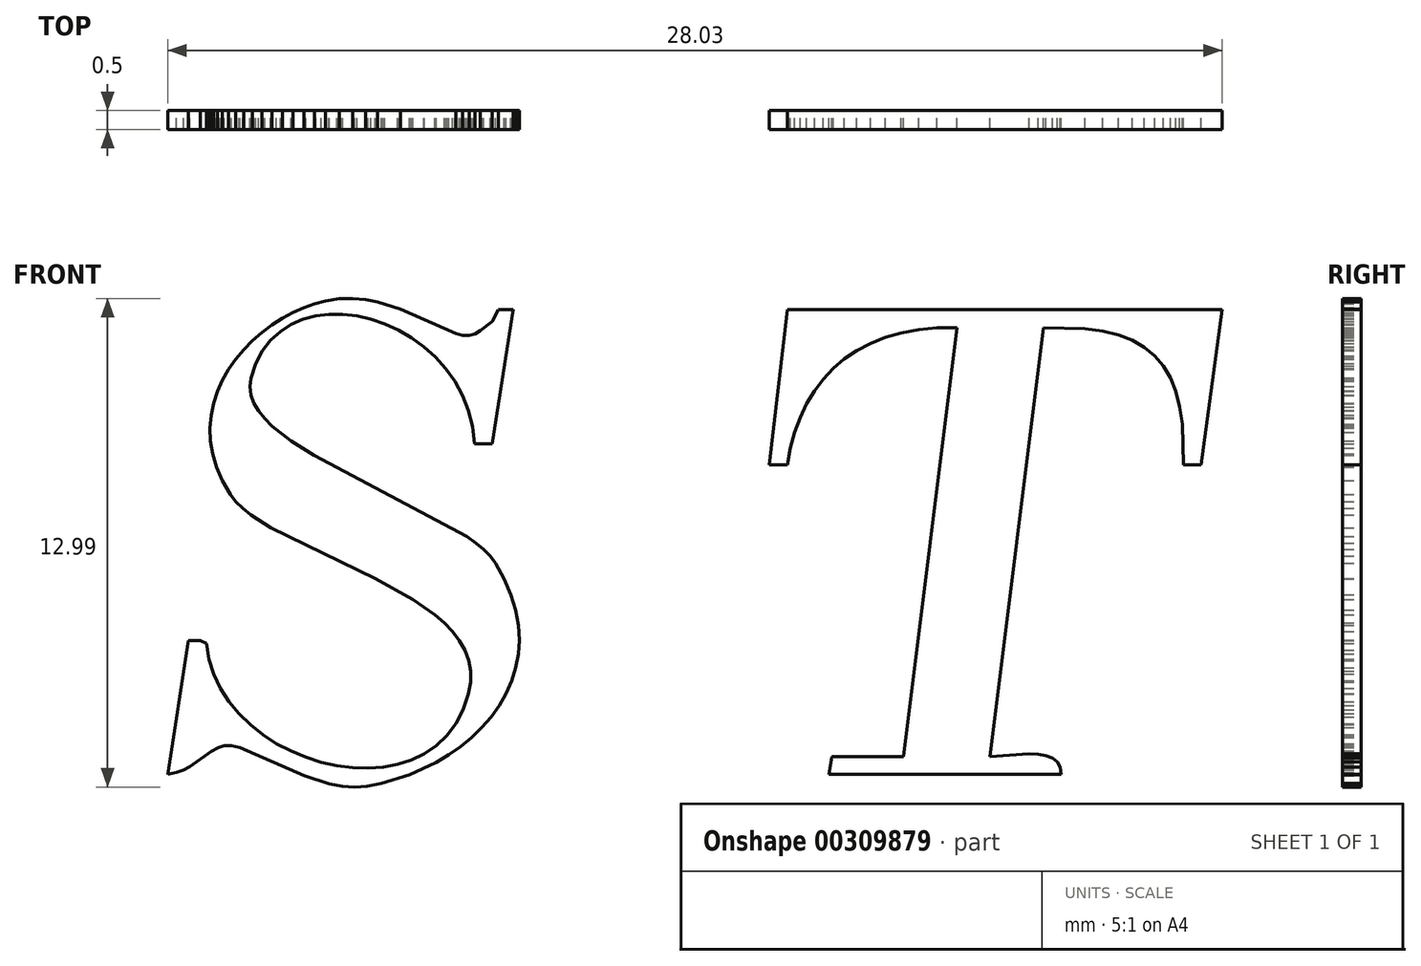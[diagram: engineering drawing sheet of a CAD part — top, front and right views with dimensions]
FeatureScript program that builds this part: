
annotation { "Feature Type Name" : "Feature", "Feature Type Description" : "" }
export const myFeature = defineFeature(function(context is Context, id is Id, definition is map)
    precondition{}
    {
        {
            var Q0;
            Q0=qCreatedBy(makeId("Front.planeOp"),FACE);
            var sketch = newSketch(context, id + "F0", { "sketchPlane" : qUnion([Q0])});
            skPoint(sketch, "E0.0", {"position": v(18.56, 6.4) * mm});
            skPoint(sketch, "E1.0", {"position": v(18, 2.28) * mm});
            skPoint(sketch, "E2.0", {"position": v(17.53, 2.28) * mm});
            skPoint(sketch, "E3.0", {"position": v(17.5, 3.36) * mm});
            skPoint(sketch, "E4.0", {"position": v(17.43, 3.82) * mm});
            skPoint(sketch, "E5.0", {"position": v(17.33, 4.23) * mm});
            skPoint(sketch, "E6.0", {"position": v(17.18, 4.6) * mm});
            skPoint(sketch, "E7.0", {"position": v(17, 4.9) * mm});
            skPoint(sketch, "E8.0", {"position": v(16.77, 5.18) * mm});
            skPoint(sketch, "E9.0", {"position": v(16.5, 5.4) * mm});
            skPoint(sketch, "E10.0", {"position": v(16.17, 5.59) * mm});
            skPoint(sketch, "E11.0", {"position": v(15.8, 5.73) * mm});
            skPoint(sketch, "E12.0", {"position": v(15.38, 5.83) * mm});
            skPoint(sketch, "E13.0", {"position": v(14.91, 5.9) * mm});
            skPoint(sketch, "E14.0", {"position": v(13.8, 5.93) * mm});
            skPoint(sketch, "E15.0", {"position": v(12.38, -5.48) * mm});
            skPoint(sketch, "E16.0", {"position": v(13.43, -5.4) * mm});
            skPoint(sketch, "E17.0", {"position": v(13.66, -5.42) * mm});
            skPoint(sketch, "E18.0", {"position": v(13.87, -5.46) * mm});
            skPoint(sketch, "E19.0", {"position": v(14.04, -5.52) * mm});
            skPoint(sketch, "E20.0", {"position": v(14.18, -5.62) * mm});
            skPoint(sketch, "E21.0", {"position": v(14.26, -5.76) * mm});
            skPoint(sketch, "E22.0", {"position": v(14.28, -5.95) * mm});
            skPoint(sketch, "E23.0", {"position": v(8.1, -5.95) * mm});
            skPoint(sketch, "E24.0", {"position": v(8.19, -5.48) * mm});
            skPoint(sketch, "E25.0", {"position": v(10.09, -5.48) * mm});
            skPoint(sketch, "E26.0", {"position": v(11.51, 5.93) * mm});
            skPoint(sketch, "E27.0", {"position": v(10.98, 5.92) * mm});
            skPoint(sketch, "E28.0", {"position": v(10.49, 5.87) * mm});
            skPoint(sketch, "E29.0", {"position": v(10.03, 5.79) * mm});
            skPoint(sketch, "E30.0", {"position": v(9.6, 5.67) * mm});
            skPoint(sketch, "E31.0", {"position": v(9.2, 5.51) * mm});
            skPoint(sketch, "E32.0", {"position": v(8.84, 5.32) * mm});
            skPoint(sketch, "E33.0", {"position": v(8.52, 5.1) * mm});
            skPoint(sketch, "E34.0", {"position": v(8.22, 4.84) * mm});
            skPoint(sketch, "E35.0", {"position": v(7.95, 4.56) * mm});
            skPoint(sketch, "E36.0", {"position": v(7.72, 4.25) * mm});
            skPoint(sketch, "E37.0", {"position": v(7.52, 3.9) * mm});
            skPoint(sketch, "E38.0", {"position": v(7.34, 3.54) * mm});
            skPoint(sketch, "E39.0", {"position": v(7.2, 3.14) * mm});
            skPoint(sketch, "E40.0", {"position": v(7.08, 2.72) * mm});
            skPoint(sketch, "E41.0", {"position": v(7, 2.28) * mm});
            skPoint(sketch, "E42.0", {"position": v(6.52, 2.28) * mm});
            skPoint(sketch, "E43.0", {"position": v(7, 6.4) * mm});
            skPoint(sketch, "E44.0", {"position": v(-0.29, 6.4) * mm});
            skPoint(sketch, "E45.0", {"position": v(-0.84, 2.84) * mm});
            skPoint(sketch, "E46.0", {"position": v(-1.32, 2.84) * mm});
            skPoint(sketch, "E47.0", {"position": v(-1.37, 3.3) * mm});
            skPoint(sketch, "E48.0", {"position": v(-1.48, 3.72) * mm});
            skPoint(sketch, "E49.0", {"position": v(-1.64, 4.13) * mm});
            skPoint(sketch, "E50.0", {"position": v(-1.84, 4.5) * mm});
            skPoint(sketch, "E51.0", {"position": v(-2.08, 4.84) * mm});
            skPoint(sketch, "E52.0", {"position": v(-2.36, 5.14) * mm});
            skPoint(sketch, "E53.0", {"position": v(-0.68, 6.4) * mm});
            skPoint(sketch, "E54.0", {"position": v(-0.84, 6.08) * mm});
            skPoint(sketch, "E55.0", {"position": v(-1.16, 5.85) * mm});
            skPoint(sketch, "E56.0", {"position": v(-1.3, 5.76) * mm});
            skPoint(sketch, "E57.0", {"position": v(-1.46, 5.72) * mm});
            skPoint(sketch, "E58.0", {"position": v(-1.63, 5.72) * mm});
            skPoint(sketch, "E59.0", {"position": v(-1.82, 5.77) * mm});
            skPoint(sketch, "E60.0", {"position": v(-3.28, 6.41) * mm});
            skPoint(sketch, "E61.0", {"position": v(-2.66, 5.42) * mm});
            skPoint(sketch, "E62.0", {"position": v(-2.99, 5.66) * mm});
            skPoint(sketch, "E63.0", {"position": v(-3.34, 5.86) * mm});
            skPoint(sketch, "E64.0", {"position": v(-3.7, 6.03) * mm});
            skPoint(sketch, "E65.0", {"position": v(-4.07, 6.15) * mm});
            skPoint(sketch, "E66.0", {"position": v(-4.44, 6.24) * mm});
            skPoint(sketch, "E67.0", {"position": v(-4.82, 6.28) * mm});
            skPoint(sketch, "E68.0", {"position": v(-4.22, 6.67) * mm});
            skPoint(sketch, "E69.0", {"position": v(-3.9, 6.61) * mm});
            skPoint(sketch, "E70.0", {"position": v(-4.56, 6.7) * mm});
            skPoint(sketch, "E71.0", {"position": v(-4.91, 6.7) * mm});
            skPoint(sketch, "E72.0", {"position": v(-5.18, 6.28) * mm});
            skPoint(sketch, "E73.0", {"position": v(-5.28, 6.64) * mm});
            skPoint(sketch, "E74.0", {"position": v(-5.57, 6.56) * mm});
            skPoint(sketch, "E75.0", {"position": v(-5.54, 6.24) * mm});
            skPoint(sketch, "E76.0", {"position": v(-5.88, 6.15) * mm});
            skPoint(sketch, "E77.0", {"position": v(-5.86, 6.46) * mm});
            skPoint(sketch, "E78.0", {"position": v(-6.14, 6.33) * mm});
            skPoint(sketch, "E79.0", {"position": v(-6.2, 6.01) * mm});
            skPoint(sketch, "E80.0", {"position": v(-6.43, 6.18) * mm});
            skPoint(sketch, "E81.0", {"position": v(-6.48, 5.83) * mm});
            skPoint(sketch, "E82.0", {"position": v(-6.7, 6) * mm});
            skPoint(sketch, "E83.0", {"position": v(-6.97, 5.8) * mm});
            skPoint(sketch, "E84.0", {"position": v(-6.73, 5.6) * mm});
            skPoint(sketch, "E85.0", {"position": v(-7.22, 5.58) * mm});
            skPoint(sketch, "E86.0", {"position": v(-6.95, 5.3) * mm});
            skPoint(sketch, "E87.0", {"position": v(-7.45, 5.35) * mm});
            skPoint(sketch, "E88.0", {"position": v(-7.13, 4.97) * mm});
            skPoint(sketch, "E89.0", {"position": v(-7.66, 5.1) * mm});
            skPoint(sketch, "E90.0", {"position": v(-7.26, 4.58) * mm});
            skPoint(sketch, "E91.0", {"position": v(-7.29, 4.36) * mm});
            skPoint(sketch, "E92.0", {"position": v(-7.26, 4.14) * mm});
            skPoint(sketch, "E93.0", {"position": v(-7.18, 3.92) * mm});
            skPoint(sketch, "E94.0", {"position": v(-7.06, 3.71) * mm});
            skPoint(sketch, "E95.0", {"position": v(-6.9, 3.5) * mm});
            skPoint(sketch, "E96.0", {"position": v(-6.7, 3.3) * mm});
            skPoint(sketch, "E97.0", {"position": v(-6.2, 2.91) * mm});
            skPoint(sketch, "E98.0", {"position": v(-5.59, 2.53) * mm});
            skPoint(sketch, "E99.0", {"position": v(-1.53, 0.38) * mm});
            skPoint(sketch, "E100.0", {"position": v(-1.28, 0.2) * mm});
            skPoint(sketch, "E101.0", {"position": v(-1.07, 0.03) * mm});
            skPoint(sketch, "E102.0", {"position": v(-0.9, -0.15) * mm});
            skPoint(sketch, "E103.0", {"position": v(-0.76, -0.33) * mm});
            skPoint(sketch, "E104.0", {"position": v(-0.53, -0.76) * mm});
            skPoint(sketch, "E105.0", {"position": v(-0.35, -1.18) * mm});
            skPoint(sketch, "E106.0", {"position": v(-0.22, -1.59) * mm});
            skPoint(sketch, "E107.0", {"position": v(-0.15, -1.99) * mm});
            skPoint(sketch, "E108.0", {"position": v(-0.13, -2.38) * mm});
            skPoint(sketch, "E109.0", {"position": v(-0.15, -2.75) * mm});
            skPoint(sketch, "E110.0", {"position": v(-0.22, -3.12) * mm});
            skPoint(sketch, "E111.0", {"position": v(-0.33, -3.47) * mm});
            skPoint(sketch, "E112.0", {"position": v(-0.48, -3.8) * mm});
            skPoint(sketch, "E113.0", {"position": v(-0.66, -4.12) * mm});
            skPoint(sketch, "E114.0", {"position": v(-0.88, -4.42) * mm});
            skPoint(sketch, "E115.0", {"position": v(-1.12, -4.7) * mm});
            skPoint(sketch, "E116.0", {"position": v(-1.4, -4.97) * mm});
            skPoint(sketch, "E117.0", {"position": v(-1.69, -5.21) * mm});
            skPoint(sketch, "E118.0", {"position": v(-2, -5.43) * mm});
            skPoint(sketch, "E119.0", {"position": v(-2.34, -5.64) * mm});
            skPoint(sketch, "E120.0", {"position": v(-3.04, -5.97) * mm});
            skPoint(sketch, "E121.0", {"position": v(-3.79, -6.2) * mm});
            skPoint(sketch, "E122.0", {"position": v(-4.17, -6.27) * mm});
            skPoint(sketch, "E123.0", {"position": v(-4.5, -6.3) * mm});
            skPoint(sketch, "E124.0", {"position": v(-4.84, -6.27) * mm});
            skPoint(sketch, "E125.0", {"position": v(-5.17, -6.2) * mm});
            skPoint(sketch, "E126.0", {"position": v(-5.84, -5.99) * mm});
            skPoint(sketch, "E127.0", {"position": v(-7.56, -5.24) * mm});
            skPoint(sketch, "E128.0", {"position": v(-6.2, -5.33) * mm});
            skPoint(sketch, "E129.0", {"position": v(-5.8, -5.5) * mm});
            skPoint(sketch, "E130.0", {"position": v(-5.4, -5.63) * mm});
            skPoint(sketch, "E131.0", {"position": v(-4.98, -5.72) * mm});
            skPoint(sketch, "E132.0", {"position": v(-4.56, -5.77) * mm});
            skPoint(sketch, "E133.0", {"position": v(-4.15, -5.79) * mm});
            skPoint(sketch, "E134.0", {"position": v(-3.75, -5.76) * mm});
            skPoint(sketch, "E135.0", {"position": v(-3.36, -5.68) * mm});
            skPoint(sketch, "E136.0", {"position": v(-3, -5.56) * mm});
            skPoint(sketch, "E137.0", {"position": v(-2.65, -5.4) * mm});
            skPoint(sketch, "E138.0", {"position": v(-2.33, -5.19) * mm});
            skPoint(sketch, "E139.0", {"position": v(-2.05, -4.92) * mm});
            skPoint(sketch, "E140.0", {"position": v(-1.81, -4.6) * mm});
            skPoint(sketch, "E141.0", {"position": v(-1.62, -4.24) * mm});
            skPoint(sketch, "E142.0", {"position": v(-1.48, -3.81) * mm});
            skPoint(sketch, "E143.0", {"position": v(-1.42, -3.5) * mm});
            skPoint(sketch, "E144.0", {"position": v(-1.42, -3.2) * mm});
            skPoint(sketch, "E145.0", {"position": v(-1.47, -2.92) * mm});
            skPoint(sketch, "E146.0", {"position": v(-1.57, -2.65) * mm});
            skPoint(sketch, "E147.0", {"position": v(-1.72, -2.4) * mm});
            skPoint(sketch, "E148.0", {"position": v(-1.9, -2.16) * mm});
            skPoint(sketch, "E149.0", {"position": v(-2.12, -1.93) * mm});
            skPoint(sketch, "E150.0", {"position": v(-2.37, -1.7) * mm});
            skPoint(sketch, "E151.0", {"position": v(-2.95, -1.3) * mm});
            skPoint(sketch, "E152.0", {"position": v(-3.96, -0.74) * mm});
            skPoint(sketch, "E153.0", {"position": v(-6.72, 0.6) * mm});
            skPoint(sketch, "E154.0", {"position": v(-7.26, 0.94) * mm});
            skPoint(sketch, "E155.0", {"position": v(-7.48, 1.12) * mm});
            skPoint(sketch, "E156.0", {"position": v(-7.67, 1.3) * mm});
            skPoint(sketch, "E157.0", {"position": v(-7.81, 1.5) * mm});
            skPoint(sketch, "E158.0", {"position": v(-8.02, 1.86) * mm});
            skPoint(sketch, "E159.0", {"position": v(-8.18, 2.22) * mm});
            skPoint(sketch, "E160.0", {"position": v(-8.28, 2.57) * mm});
            skPoint(sketch, "E161.0", {"position": v(-8.34, 2.92) * mm});
            skPoint(sketch, "E162.0", {"position": v(-8.35, 3.26) * mm});
            skPoint(sketch, "E163.0", {"position": v(-8.32, 3.6) * mm});
            skPoint(sketch, "E164.0", {"position": v(-8.25, 3.92) * mm});
            skPoint(sketch, "E165.0", {"position": v(-8.15, 4.23) * mm});
            skPoint(sketch, "E166.0", {"position": v(-8.02, 4.53) * mm});
            skPoint(sketch, "E167.0", {"position": v(-7.85, 4.82) * mm});
            skPoint(sketch, "E168.0", {"position": v(-7.77, -5.2) * mm});
            skPoint(sketch, "E169.0", {"position": v(-7.97, -5.19) * mm});
            skPoint(sketch, "E170.0", {"position": v(-8.13, -5.24) * mm});
            skPoint(sketch, "E171.0", {"position": v(-8.3, -5.34) * mm});
            skPoint(sketch, "E172.0", {"position": v(-8.89, -5.75) * mm});
            skPoint(sketch, "E173.0", {"position": v(-9.05, -5.83) * mm});
            skPoint(sketch, "E174.0", {"position": v(-9.24, -5.9) * mm});
            skPoint(sketch, "E175.0", {"position": v(-9.47, -5.95) * mm});
            skPoint(sketch, "E176.0", {"position": v(-8.92, -2.39) * mm});
            skPoint(sketch, "E177.0", {"position": v(-8.6, -2.39) * mm});
            skPoint(sketch, "E178.0", {"position": v(-8.45, -2.47) * mm});
            skPoint(sketch, "E179.0", {"position": v(-8.38, -2.89) * mm});
            skPoint(sketch, "E180.0", {"position": v(-8.25, -3.29) * mm});
            skPoint(sketch, "E181.0", {"position": v(-8.07, -3.66) * mm});
            skPoint(sketch, "E182.0", {"position": v(-7.85, -4.01) * mm});
            skPoint(sketch, "E183.0", {"position": v(-7.58, -4.34) * mm});
            skPoint(sketch, "E184.0", {"position": v(-7.28, -4.63) * mm});
            skPoint(sketch, "E185.0", {"position": v(-6.94, -4.9) * mm});
            skPoint(sketch, "E186.0", {"position": v(-6.58, -5.13) * mm});
            skLineSegment(sketch, "E187", {"start": v(7, 6.4) * mm, "end": v(18.56, 6.4) * mm});
            skLineSegment(sketch, "E188", {"start": v(18.56, 6.4) * mm, "end": v(18, 2.28) * mm});
            skLineSegment(sketch, "E189", {"start": v(18, 2.28) * mm, "end": v(17.53, 2.28) * mm});
            skLineSegment(sketch, "E190", {"start": v(17.53, 2.28) * mm, "end": v(17.5, 3.36) * mm});
            skLineSegment(sketch, "E191", {"start": v(17.5, 3.36) * mm, "end": v(17.43, 3.82) * mm});
            skLineSegment(sketch, "E192", {"start": v(17.43, 3.82) * mm, "end": v(17.33, 4.23) * mm});
            skLineSegment(sketch, "E193", {"start": v(17.33, 4.23) * mm, "end": v(17.18, 4.6) * mm});
            skLineSegment(sketch, "E194", {"start": v(17.18, 4.6) * mm, "end": v(17, 4.9) * mm});
            skLineSegment(sketch, "E195", {"start": v(17, 4.9) * mm, "end": v(16.77, 5.18) * mm});
            skLineSegment(sketch, "E196", {"start": v(16.77, 5.18) * mm, "end": v(16.5, 5.4) * mm});
            skLineSegment(sketch, "E197", {"start": v(16.5, 5.4) * mm, "end": v(16.17, 5.59) * mm});
            skLineSegment(sketch, "E198", {"start": v(16.17, 5.59) * mm, "end": v(15.8, 5.73) * mm});
            skLineSegment(sketch, "E199", {"start": v(15.8, 5.73) * mm, "end": v(15.38, 5.83) * mm});
            skLineSegment(sketch, "E200", {"start": v(15.38, 5.83) * mm, "end": v(14.91, 5.9) * mm});
            skLineSegment(sketch, "E201", {"start": v(14.91, 5.9) * mm, "end": v(13.8, 5.93) * mm});
            skLineSegment(sketch, "E202", {"start": v(13.8, 5.93) * mm, "end": v(12.38, -5.48) * mm});
            skLineSegment(sketch, "E203", {"start": v(12.38, -5.48) * mm, "end": v(13.43, -5.4) * mm});
            skLineSegment(sketch, "E204", {"start": v(13.43, -5.4) * mm, "end": v(13.66, -5.42) * mm});
            skLineSegment(sketch, "E205", {"start": v(13.66, -5.42) * mm, "end": v(13.87, -5.46) * mm});
            skLineSegment(sketch, "E206", {"start": v(13.87, -5.46) * mm, "end": v(14.04, -5.52) * mm});
            skLineSegment(sketch, "E207", {"start": v(14.04, -5.52) * mm, "end": v(14.18, -5.62) * mm});
            skLineSegment(sketch, "E208", {"start": v(14.18, -5.62) * mm, "end": v(14.26, -5.76) * mm});
            skLineSegment(sketch, "E209", {"start": v(14.26, -5.76) * mm, "end": v(14.28, -5.95) * mm});
            skLineSegment(sketch, "E210", {"start": v(14.28, -5.95) * mm, "end": v(8.1, -5.95) * mm});
            skLineSegment(sketch, "E211", {"start": v(8.1, -5.95) * mm, "end": v(8.19, -5.48) * mm});
            skLineSegment(sketch, "E212", {"start": v(8.19, -5.48) * mm, "end": v(10.09, -5.48) * mm});
            skLineSegment(sketch, "E213", {"start": v(11.51, 5.93) * mm, "end": v(10.09, -5.48) * mm});
            skLineSegment(sketch, "E214", {"start": v(11.51, 5.93) * mm, "end": v(10.98, 5.92) * mm});
            skLineSegment(sketch, "E215", {"start": v(10.98, 5.92) * mm, "end": v(10.49, 5.87) * mm});
            skLineSegment(sketch, "E216", {"start": v(10.49, 5.87) * mm, "end": v(10.03, 5.79) * mm});
            skLineSegment(sketch, "E217", {"start": v(10.03, 5.79) * mm, "end": v(9.6, 5.67) * mm});
            skLineSegment(sketch, "E218", {"start": v(9.6, 5.67) * mm, "end": v(9.2, 5.51) * mm});
            skLineSegment(sketch, "E219", {"start": v(9.2, 5.51) * mm, "end": v(8.84, 5.32) * mm});
            skLineSegment(sketch, "E220", {"start": v(8.84, 5.32) * mm, "end": v(8.52, 5.1) * mm});
            skLineSegment(sketch, "E221", {"start": v(8.52, 5.1) * mm, "end": v(8.22, 4.84) * mm});
            skLineSegment(sketch, "E222", {"start": v(8.22, 4.84) * mm, "end": v(7.95, 4.56) * mm});
            skLineSegment(sketch, "E223", {"start": v(7.95, 4.56) * mm, "end": v(7.72, 4.25) * mm});
            skLineSegment(sketch, "E224", {"start": v(7.72, 4.25) * mm, "end": v(7.52, 3.9) * mm});
            skLineSegment(sketch, "E225", {"start": v(7.52, 3.9) * mm, "end": v(7.34, 3.54) * mm});
            skLineSegment(sketch, "E226", {"start": v(7.34, 3.54) * mm, "end": v(7.2, 3.14) * mm});
            skLineSegment(sketch, "E227", {"start": v(7.2, 3.14) * mm, "end": v(7.08, 2.72) * mm});
            skLineSegment(sketch, "E228", {"start": v(7.08, 2.72) * mm, "end": v(7, 2.28) * mm});
            skLineSegment(sketch, "E229", {"start": v(7, 2.28) * mm, "end": v(6.52, 2.28) * mm});
            skLineSegment(sketch, "E230", {"start": v(7, 6.4) * mm, "end": v(6.52, 2.28) * mm});
            skLineSegment(sketch, "E231", {"start": v(-0.29, 6.4) * mm, "end": v(-0.84, 2.84) * mm});
            skLineSegment(sketch, "E232", {"start": v(-0.84, 2.84) * mm, "end": v(-1.32, 2.84) * mm});
            skLineSegment(sketch, "E233", {"start": v(-1.32, 2.84) * mm, "end": v(-1.37, 3.3) * mm});
            skLineSegment(sketch, "E234", {"start": v(-1.37, 3.3) * mm, "end": v(-1.48, 3.72) * mm});
            skLineSegment(sketch, "E235", {"start": v(-1.48, 3.72) * mm, "end": v(-1.64, 4.13) * mm});
            skLineSegment(sketch, "E236", {"start": v(-1.64, 4.13) * mm, "end": v(-1.84, 4.5) * mm});
            skLineSegment(sketch, "E237", {"start": v(-1.84, 4.5) * mm, "end": v(-2.08, 4.84) * mm});
            skLineSegment(sketch, "E238", {"start": v(-2.08, 4.84) * mm, "end": v(-2.36, 5.14) * mm});
            skLineSegment(sketch, "E239", {"start": v(-2.36, 5.14) * mm, "end": v(-2.66, 5.42) * mm});
            skLineSegment(sketch, "E240", {"start": v(-0.29, 6.4) * mm, "end": v(-0.68, 6.4) * mm});
            skLineSegment(sketch, "E241", {"start": v(-0.68, 6.4) * mm, "end": v(-0.84, 6.08) * mm});
            skLineSegment(sketch, "E242", {"start": v(-0.84, 6.08) * mm, "end": v(-1.16, 5.85) * mm});
            skLineSegment(sketch, "E243", {"start": v(-1.16, 5.85) * mm, "end": v(-1.3, 5.76) * mm});
            skLineSegment(sketch, "E244", {"start": v(-1.3, 5.76) * mm, "end": v(-1.46, 5.72) * mm});
            skLineSegment(sketch, "E245", {"start": v(-1.46, 5.72) * mm, "end": v(-1.63, 5.72) * mm});
            skLineSegment(sketch, "E246", {"start": v(-1.63, 5.72) * mm, "end": v(-1.82, 5.77) * mm});
            skLineSegment(sketch, "E247", {"start": v(-1.82, 5.77) * mm, "end": v(-3.28, 6.41) * mm});
            skLineSegment(sketch, "E248", {"start": v(-3.28, 6.41) * mm, "end": v(-3.9, 6.61) * mm});
            skLineSegment(sketch, "E249", {"start": v(-3.9, 6.61) * mm, "end": v(-4.22, 6.67) * mm});
            skLineSegment(sketch, "E250", {"start": v(-4.22, 6.67) * mm, "end": v(-4.56, 6.7) * mm});
            skLineSegment(sketch, "E251", {"start": v(-4.56, 6.7) * mm, "end": v(-4.91, 6.7) * mm});
            skLineSegment(sketch, "E252", {"start": v(-4.91, 6.7) * mm, "end": v(-5.28, 6.64) * mm});
            skLineSegment(sketch, "E253", {"start": v(-5.28, 6.64) * mm, "end": v(-5.57, 6.56) * mm});
            skLineSegment(sketch, "E254", {"start": v(-5.57, 6.56) * mm, "end": v(-5.86, 6.46) * mm});
            skLineSegment(sketch, "E255", {"start": v(-5.86, 6.46) * mm, "end": v(-6.14, 6.33) * mm});
            skLineSegment(sketch, "E256", {"start": v(-6.14, 6.33) * mm, "end": v(-6.43, 6.18) * mm});
            skLineSegment(sketch, "E257", {"start": v(-6.43, 6.18) * mm, "end": v(-6.7, 6) * mm});
            skLineSegment(sketch, "E258", {"start": v(-6.7, 6) * mm, "end": v(-6.97, 5.8) * mm});
            skLineSegment(sketch, "E259", {"start": v(-6.97, 5.8) * mm, "end": v(-7.22, 5.58) * mm});
            skLineSegment(sketch, "E260", {"start": v(-7.22, 5.58) * mm, "end": v(-7.45, 5.35) * mm});
            skLineSegment(sketch, "E261", {"start": v(-7.45, 5.35) * mm, "end": v(-7.66, 5.1) * mm});
            skLineSegment(sketch, "E262", {"start": v(-7.66, 5.1) * mm, "end": v(-7.85, 4.82) * mm});
            skLineSegment(sketch, "E263", {"start": v(-7.85, 4.82) * mm, "end": v(-8.02, 4.53) * mm});
            skLineSegment(sketch, "E264", {"start": v(-8.02, 4.53) * mm, "end": v(-8.15, 4.23) * mm});
            skLineSegment(sketch, "E265", {"start": v(-8.15, 4.23) * mm, "end": v(-8.25, 3.92) * mm});
            skLineSegment(sketch, "E266", {"start": v(-8.25, 3.92) * mm, "end": v(-8.32, 3.6) * mm});
            skLineSegment(sketch, "E267", {"start": v(-8.32, 3.6) * mm, "end": v(-8.35, 3.26) * mm});
            skLineSegment(sketch, "E268", {"start": v(-8.35, 3.26) * mm, "end": v(-8.34, 2.92) * mm});
            skLineSegment(sketch, "E269", {"start": v(-8.34, 2.92) * mm, "end": v(-8.28, 2.57) * mm});
            skLineSegment(sketch, "E270", {"start": v(-8.28, 2.57) * mm, "end": v(-8.18, 2.22) * mm});
            skLineSegment(sketch, "E271", {"start": v(-8.18, 2.22) * mm, "end": v(-8.02, 1.86) * mm});
            skLineSegment(sketch, "E272", {"start": v(-8.02, 1.86) * mm, "end": v(-7.81, 1.5) * mm});
            skLineSegment(sketch, "E273", {"start": v(-7.81, 1.5) * mm, "end": v(-7.67, 1.3) * mm});
            skLineSegment(sketch, "E274", {"start": v(-7.67, 1.3) * mm, "end": v(-7.48, 1.12) * mm});
            skLineSegment(sketch, "E275", {"start": v(-7.48, 1.12) * mm, "end": v(-7.26, 0.94) * mm});
            skLineSegment(sketch, "E276", {"start": v(-7.26, 0.94) * mm, "end": v(-6.72, 0.6) * mm});
            skLineSegment(sketch, "E277", {"start": v(-6.72, 0.6) * mm, "end": v(-3.96, -0.74) * mm});
            skLineSegment(sketch, "E278", {"start": v(-3.96, -0.74) * mm, "end": v(-2.95, -1.3) * mm});
            skLineSegment(sketch, "E279", {"start": v(-2.95, -1.3) * mm, "end": v(-2.37, -1.7) * mm});
            skLineSegment(sketch, "E280", {"start": v(-2.37, -1.7) * mm, "end": v(-2.12, -1.93) * mm});
            skLineSegment(sketch, "E281", {"start": v(-2.66, 5.42) * mm, "end": v(-2.99, 5.66) * mm});
            skLineSegment(sketch, "E282", {"start": v(-2.99, 5.66) * mm, "end": v(-3.34, 5.86) * mm});
            skLineSegment(sketch, "E283", {"start": v(-3.34, 5.86) * mm, "end": v(-3.7, 6.03) * mm});
            skLineSegment(sketch, "E284", {"start": v(-3.7, 6.03) * mm, "end": v(-4.07, 6.15) * mm});
            skLineSegment(sketch, "E285", {"start": v(-4.07, 6.15) * mm, "end": v(-4.44, 6.24) * mm});
            skLineSegment(sketch, "E286", {"start": v(-4.44, 6.24) * mm, "end": v(-4.82, 6.28) * mm});
            skLineSegment(sketch, "E287", {"start": v(-4.82, 6.28) * mm, "end": v(-5.18, 6.28) * mm});
            skLineSegment(sketch, "E288", {"start": v(-5.18, 6.28) * mm, "end": v(-5.54, 6.24) * mm});
            skLineSegment(sketch, "E289", {"start": v(-5.54, 6.24) * mm, "end": v(-5.88, 6.15) * mm});
            skLineSegment(sketch, "E290", {"start": v(-5.88, 6.15) * mm, "end": v(-6.2, 6.01) * mm});
            skLineSegment(sketch, "E291", {"start": v(-6.2, 6.01) * mm, "end": v(-6.48, 5.83) * mm});
            skLineSegment(sketch, "E292", {"start": v(-6.48, 5.83) * mm, "end": v(-6.73, 5.6) * mm});
            skLineSegment(sketch, "E293", {"start": v(-6.73, 5.6) * mm, "end": v(-6.95, 5.3) * mm});
            skLineSegment(sketch, "E294", {"start": v(-6.95, 5.3) * mm, "end": v(-7.13, 4.97) * mm});
            skLineSegment(sketch, "E295", {"start": v(-7.13, 4.97) * mm, "end": v(-7.26, 4.58) * mm});
            skLineSegment(sketch, "E296", {"start": v(-7.26, 4.58) * mm, "end": v(-7.29, 4.36) * mm});
            skLineSegment(sketch, "E297", {"start": v(-7.29, 4.36) * mm, "end": v(-7.26, 4.14) * mm});
            skLineSegment(sketch, "E298", {"start": v(-7.26, 4.14) * mm, "end": v(-7.18, 3.92) * mm});
            skLineSegment(sketch, "E299", {"start": v(-7.18, 3.92) * mm, "end": v(-7.06, 3.71) * mm});
            skLineSegment(sketch, "E300", {"start": v(-7.06, 3.71) * mm, "end": v(-6.9, 3.5) * mm});
            skLineSegment(sketch, "E301", {"start": v(-6.9, 3.5) * mm, "end": v(-6.7, 3.3) * mm});
            skLineSegment(sketch, "E302", {"start": v(-6.7, 3.3) * mm, "end": v(-6.2, 2.91) * mm});
            skLineSegment(sketch, "E303", {"start": v(-6.2, 2.91) * mm, "end": v(-5.59, 2.53) * mm});
            skLineSegment(sketch, "E304", {"start": v(-5.59, 2.53) * mm, "end": v(-1.53, 0.38) * mm});
            skLineSegment(sketch, "E305", {"start": v(-1.53, 0.38) * mm, "end": v(-1.28, 0.2) * mm});
            skLineSegment(sketch, "E306", {"start": v(-1.28, 0.2) * mm, "end": v(-1.07, 0.03) * mm});
            skLineSegment(sketch, "E307", {"start": v(-1.07, 0.03) * mm, "end": v(-0.9, -0.15) * mm});
            skLineSegment(sketch, "E308", {"start": v(-0.9, -0.15) * mm, "end": v(-0.76, -0.33) * mm});
            skLineSegment(sketch, "E309", {"start": v(-0.76, -0.33) * mm, "end": v(-0.53, -0.76) * mm});
            skLineSegment(sketch, "E310", {"start": v(-0.53, -0.76) * mm, "end": v(-0.35, -1.18) * mm});
            skLineSegment(sketch, "E311", {"start": v(-0.35, -1.18) * mm, "end": v(-0.22, -1.59) * mm});
            skLineSegment(sketch, "E312", {"start": v(-0.22, -1.59) * mm, "end": v(-0.15, -1.99) * mm});
            skLineSegment(sketch, "E313", {"start": v(-0.15, -1.99) * mm, "end": v(-0.13, -2.38) * mm});
            skLineSegment(sketch, "E314", {"start": v(-0.13, -2.38) * mm, "end": v(-0.15, -2.75) * mm});
            skLineSegment(sketch, "E315", {"start": v(-0.15, -2.75) * mm, "end": v(-0.22, -3.12) * mm});
            skLineSegment(sketch, "E316", {"start": v(-0.22, -3.12) * mm, "end": v(-0.33, -3.47) * mm});
            skLineSegment(sketch, "E317", {"start": v(-0.33, -3.47) * mm, "end": v(-0.48, -3.8) * mm});
            skLineSegment(sketch, "E318", {"start": v(-0.48, -3.8) * mm, "end": v(-0.66, -4.12) * mm});
            skLineSegment(sketch, "E319", {"start": v(-0.66, -4.12) * mm, "end": v(-0.88, -4.42) * mm});
            skLineSegment(sketch, "E320", {"start": v(-0.88, -4.42) * mm, "end": v(-1.12, -4.7) * mm});
            skLineSegment(sketch, "E321", {"start": v(-2.12, -1.93) * mm, "end": v(-1.9, -2.16) * mm});
            skLineSegment(sketch, "E322", {"start": v(-1.9, -2.16) * mm, "end": v(-1.72, -2.4) * mm});
            skLineSegment(sketch, "E323", {"start": v(-1.72, -2.4) * mm, "end": v(-1.57, -2.65) * mm});
            skLineSegment(sketch, "E324", {"start": v(-1.57, -2.65) * mm, "end": v(-1.47, -2.92) * mm});
            skLineSegment(sketch, "E325", {"start": v(-1.47, -2.92) * mm, "end": v(-1.42, -3.2) * mm});
            skLineSegment(sketch, "E326", {"start": v(-1.42, -3.2) * mm, "end": v(-1.42, -3.5) * mm});
            skLineSegment(sketch, "E327", {"start": v(-1.42, -3.5) * mm, "end": v(-1.48, -3.81) * mm});
            skLineSegment(sketch, "E328", {"start": v(-1.48, -3.81) * mm, "end": v(-1.62, -4.24) * mm});
            skLineSegment(sketch, "E329", {"start": v(-1.12, -4.7) * mm, "end": v(-1.4, -4.97) * mm});
            skLineSegment(sketch, "E330", {"start": v(-1.4, -4.97) * mm, "end": v(-1.69, -5.21) * mm});
            skLineSegment(sketch, "E331", {"start": v(-1.69, -5.21) * mm, "end": v(-2, -5.43) * mm});
            skLineSegment(sketch, "E332", {"start": v(-1.62, -4.24) * mm, "end": v(-1.81, -4.6) * mm});
            skLineSegment(sketch, "E333", {"start": v(-1.81, -4.6) * mm, "end": v(-2.05, -4.92) * mm});
            skLineSegment(sketch, "E334", {"start": v(-2.05, -4.92) * mm, "end": v(-2.33, -5.19) * mm});
            skLineSegment(sketch, "E335", {"start": v(-2.33, -5.19) * mm, "end": v(-2.65, -5.4) * mm});
            skLineSegment(sketch, "E336", {"start": v(-2.65, -5.4) * mm, "end": v(-3, -5.56) * mm});
            skLineSegment(sketch, "E337", {"start": v(-2, -5.43) * mm, "end": v(-2.34, -5.64) * mm});
            skLineSegment(sketch, "E338", {"start": v(-2.34, -5.64) * mm, "end": v(-3.04, -5.97) * mm});
            skLineSegment(sketch, "E339", {"start": v(-3, -5.56) * mm, "end": v(-3.36, -5.68) * mm});
            skLineSegment(sketch, "E340", {"start": v(-3.79, -6.2) * mm, "end": v(-3.04, -5.97) * mm});
            skLineSegment(sketch, "E341", {"start": v(-3.36, -5.68) * mm, "end": v(-3.75, -5.76) * mm});
            skLineSegment(sketch, "E342", {"start": v(-4.56, -5.77) * mm, "end": v(-4.98, -5.72) * mm});
            skLineSegment(sketch, "E343", {"start": v(-3.79, -6.2) * mm, "end": v(-4.17, -6.27) * mm});
            skLineSegment(sketch, "E344", {"start": v(-4.17, -6.27) * mm, "end": v(-4.5, -6.3) * mm});
            skLineSegment(sketch, "E345", {"start": v(-5.84, -5.99) * mm, "end": v(-5.17, -6.2) * mm});
            skLineSegment(sketch, "E346", {"start": v(-5.17, -6.2) * mm, "end": v(-4.84, -6.27) * mm});
            skLineSegment(sketch, "E347", {"start": v(-4.84, -6.27) * mm, "end": v(-4.5, -6.3) * mm});
            skLineSegment(sketch, "E348", {"start": v(-4.98, -5.72) * mm, "end": v(-5.4, -5.63) * mm});
            skLineSegment(sketch, "E349", {"start": v(-5.4, -5.63) * mm, "end": v(-5.8, -5.5) * mm});
            skLineSegment(sketch, "E350", {"start": v(-5.8, -5.5) * mm, "end": v(-6.2, -5.33) * mm});
            skLineSegment(sketch, "E351", {"start": v(-6.2, -5.33) * mm, "end": v(-6.58, -5.13) * mm});
            skLineSegment(sketch, "E352", {"start": v(-8.45, -2.47) * mm, "end": v(-8.38, -2.89) * mm});
            skLineSegment(sketch, "E353", {"start": v(-8.38, -2.89) * mm, "end": v(-8.25, -3.29) * mm});
            skLineSegment(sketch, "E354", {"start": v(-8.25, -3.29) * mm, "end": v(-8.07, -3.66) * mm});
            skLineSegment(sketch, "E355", {"start": v(-8.07, -3.66) * mm, "end": v(-7.85, -4.01) * mm});
            skLineSegment(sketch, "E356", {"start": v(-7.85, -4.01) * mm, "end": v(-7.58, -4.34) * mm});
            skLineSegment(sketch, "E357", {"start": v(-7.58, -4.34) * mm, "end": v(-7.28, -4.63) * mm});
            skLineSegment(sketch, "E358", {"start": v(-7.28, -4.63) * mm, "end": v(-6.94, -4.9) * mm});
            skLineSegment(sketch, "E359", {"start": v(-6.94, -4.9) * mm, "end": v(-6.58, -5.13) * mm});
            skLineSegment(sketch, "E360", {"start": v(-8.45, -2.47) * mm, "end": v(-8.6, -2.39) * mm});
            skLineSegment(sketch, "E361", {"start": v(-8.92, -2.39) * mm, "end": v(-8.6, -2.39) * mm});
            skLineSegment(sketch, "E362", {"start": v(-8.92, -2.39) * mm, "end": v(-9.47, -5.95) * mm});
            skLineSegment(sketch, "E363", {"start": v(-9.47, -5.95) * mm, "end": v(-9.24, -5.9) * mm});
            skLineSegment(sketch, "E364", {"start": v(-9.24, -5.9) * mm, "end": v(-9.05, -5.83) * mm});
            skLineSegment(sketch, "E365", {"start": v(-9.05, -5.83) * mm, "end": v(-8.89, -5.75) * mm});
            skLineSegment(sketch, "E366", {"start": v(-8.89, -5.75) * mm, "end": v(-8.3, -5.34) * mm});
            skLineSegment(sketch, "E367", {"start": v(-8.3, -5.34) * mm, "end": v(-8.13, -5.24) * mm});
            skLineSegment(sketch, "E368", {"start": v(-8.13, -5.24) * mm, "end": v(-7.97, -5.19) * mm});
            skLineSegment(sketch, "E369", {"start": v(-7.97, -5.19) * mm, "end": v(-7.77, -5.2) * mm});
            skLineSegment(sketch, "E370", {"start": v(-7.77, -5.2) * mm, "end": v(-7.56, -5.24) * mm});
            skLineSegment(sketch, "E371", {"start": v(-7.56, -5.24) * mm, "end": v(-5.84, -5.99) * mm});
            skLineSegment(sketch, "E372", {"start": v(-4.56, -5.77) * mm, "end": v(-4.15, -5.79) * mm});
            skLineSegment(sketch, "E373", {"start": v(-4.15, -5.79) * mm, "end": v(-3.75, -5.76) * mm});
            skSolve(sketch);
        }
        {
            var Q0;
            Q0=makeQuery(id+"F0.imprint","IMPRINT",FACE,{"disambiguationData":[TD([[makeQuery(id+"F0.imprint","IMPRINT",EDGE,{"derivedFrom":sQuery(id+"F0.wireOp",EDGE,"E231")}),-1.0]])]});
            var Q1;
            Q1=makeQuery(id+"F0.imprint","IMPRINT",FACE,{"disambiguationData":[TD([[makeQuery(id+"F0.imprint","IMPRINT",EDGE,{"derivedFrom":sQuery(id+"F0.wireOp",EDGE,"E187")}),-1.0]])]});
            extrude(context, id + "F1", {"entities" : qUnion([Q0, Q1]), "depth" : 0.5 * mm});
        }
    });
